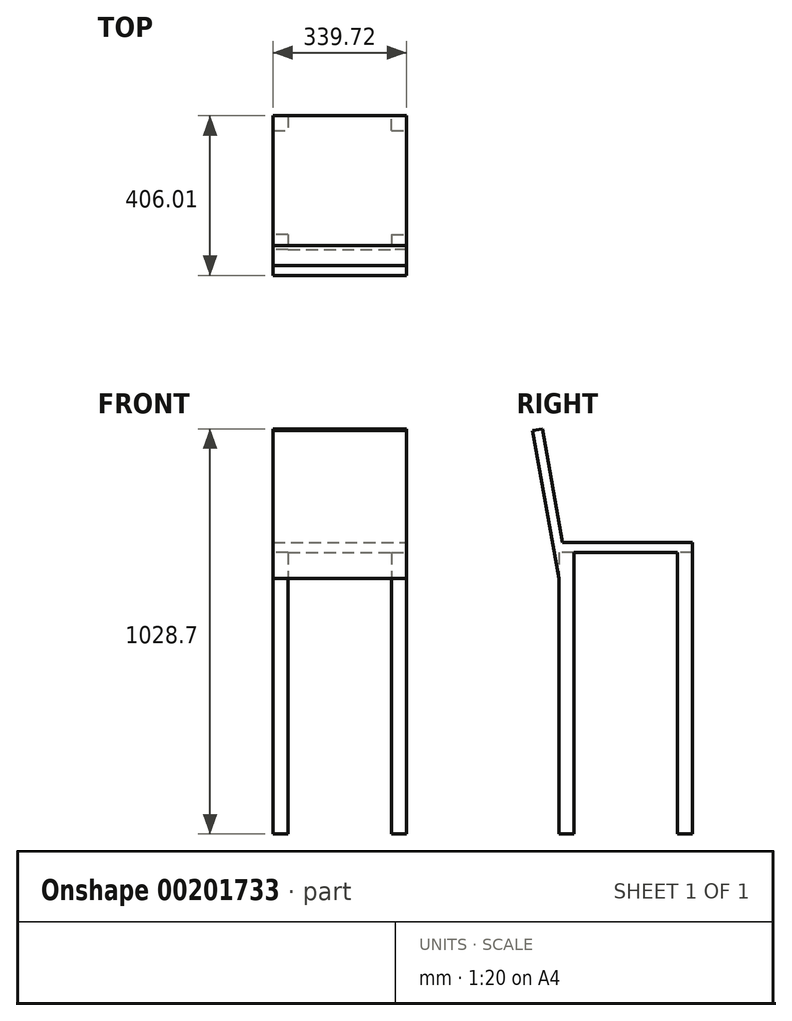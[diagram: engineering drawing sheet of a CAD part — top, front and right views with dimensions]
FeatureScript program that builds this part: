
annotation { "Feature Type Name" : "Feature", "Feature Type Description" : "" }
export const myFeature = defineFeature(function(context is Context, id is Id, definition is map)
    precondition{}
    {
        {
            var Q0;
            Q0=qCreatedBy(makeId("Top.planeOp"),FACE);
            var sketch = newSketch(context, id + "F0", { "sketchPlane" : qUnion([Q0])});
            skLineSegment(sketch, "E0.bottom", {"start": v(169.86, -169.86) * mm, "end": v(-169.86, -169.86) * mm, "construction": true});
            skLineSegment(sketch, "E0.top", {"start": v(169.86, 169.86) * mm, "end": v(-169.86, 169.86) * mm, "construction": true});
            skLineSegment(sketch, "E0.left", {"start": v(169.86, -169.86) * mm, "end": v(169.86, 169.86) * mm, "construction": true});
            skLineSegment(sketch, "E0.right", {"start": v(-169.86, -169.86) * mm, "end": v(-169.86, 169.86) * mm, "construction": true});
            skPoint(sketch, "E0.middle", {"position": v(0, 0) * mm});
            skLineSegment(sketch, "E1.bottom", {"start": v(-169.86, 169.86) * mm, "end": v(-131.76, 169.86) * mm});
            skLineSegment(sketch, "E1.top", {"start": v(-169.86, 131.76) * mm, "end": v(-131.76, 131.76) * mm});
            skLineSegment(sketch, "E1.left", {"start": v(-169.86, 169.86) * mm, "end": v(-169.86, 131.76) * mm});
            skLineSegment(sketch, "E1.right", {"start": v(-131.76, 169.86) * mm, "end": v(-131.76, 131.76) * mm});
            skLineSegment(sketch, "E2.bottom", {"start": v(-169.86, -169.86) * mm, "end": v(-131.76, -169.86) * mm});
            skLineSegment(sketch, "E2.top", {"start": v(-169.86, -131.76) * mm, "end": v(-131.76, -131.76) * mm});
            skLineSegment(sketch, "E2.left", {"start": v(-169.86, -169.86) * mm, "end": v(-169.86, -131.76) * mm});
            skLineSegment(sketch, "E2.right", {"start": v(-131.76, -169.86) * mm, "end": v(-131.76, -131.76) * mm});
            skLineSegment(sketch, "E3.bottom", {"start": v(169.86, -169.86) * mm, "end": v(131.76, -169.86) * mm});
            skLineSegment(sketch, "E3.top", {"start": v(169.86, -131.76) * mm, "end": v(131.76, -131.76) * mm});
            skLineSegment(sketch, "E3.left", {"start": v(169.86, -169.86) * mm, "end": v(169.86, -131.76) * mm});
            skLineSegment(sketch, "E3.right", {"start": v(131.76, -169.86) * mm, "end": v(131.76, -131.76) * mm});
            skLineSegment(sketch, "E4.bottom", {"start": v(169.86, 169.86) * mm, "end": v(131.76, 169.86) * mm});
            skLineSegment(sketch, "E4.top", {"start": v(169.86, 131.76) * mm, "end": v(131.76, 131.76) * mm});
            skLineSegment(sketch, "E4.left", {"start": v(169.86, 169.86) * mm, "end": v(169.86, 131.76) * mm});
            skLineSegment(sketch, "E4.right", {"start": v(131.76, 169.86) * mm, "end": v(131.76, 131.76) * mm});
            skSolve(sketch);
        }
        {
            var Q0;
            Q0=makeQuery(id+"F0.imprint","IMPRINT",FACE,{"disambiguationData":[TD([[makeQuery(id+"F0.imprint","IMPRINT",EDGE,{"derivedFrom":sQuery(id+"F0.wireOp",EDGE,"E1.bottom")}),-1.0]])]});
            var Q1;
            Q1=makeQuery(id+"F0.imprint","IMPRINT",FACE,{"disambiguationData":[TD([[makeQuery(id+"F0.imprint","IMPRINT",EDGE,{"derivedFrom":sQuery(id+"F0.wireOp",EDGE,"E2.bottom")}),1.0]])]});
            var Q2;
            Q2=makeQuery(id+"F0.imprint","IMPRINT",FACE,{"disambiguationData":[TD([[makeQuery(id+"F0.imprint","IMPRINT",EDGE,{"derivedFrom":sQuery(id+"F0.wireOp",EDGE,"E3.bottom")}),-1.0]])]});
            var Q3;
            Q3=makeQuery(id+"F0.imprint","IMPRINT",FACE,{"disambiguationData":[TD([[makeQuery(id+"F0.imprint","IMPRINT",EDGE,{"derivedFrom":sQuery(id+"F0.wireOp",EDGE,"E4.bottom")}),1.0]])]});
            extrude(context, id + "F1", {"entities" : qUnion([Q0, Q1, Q2, Q3]), "depth" : 739.77 * mm});
        }
        {
            var Q0;
            Q0=makeQuery(id+"F1.opExtrude","CAP_FACE",FACE,{"disambiguationData":[OSD([sQuery(id+"F0.wireOp",EDGE,"E1.bottom"),sQuery(id+"F0.wireOp",EDGE,"E1.top"),sQuery(id+"F0.wireOp",EDGE,"E1.left"),sQuery(id+"F0.wireOp",EDGE,"E1.right")])],"isStart":false});
            var sketch = newSketch(context, id + "F2", { "sketchPlane" : qUnion([Q0])});
            skPoint(sketch, "E5.0", {"position": v(-169.86, 150.81) * mm});
            skPoint(sketch, "E6.0", {"position": v(-169.86, 169.86) * mm});
            skPoint(sketch, "E7.0", {"position": v(-169.86, -169.86) * mm});
            skPoint(sketch, "E8.0", {"position": v(169.86, -169.86) * mm});
            skPoint(sketch, "E9.0", {"position": v(169.86, 169.86) * mm});
            skLineSegment(sketch, "E10.bottom", {"start": v(-169.86, 169.86) * mm, "end": v(169.86, 169.86) * mm});
            skLineSegment(sketch, "E10.top", {"start": v(-169.86, -169.86) * mm, "end": v(169.86, -169.86) * mm});
            skLineSegment(sketch, "E10.left", {"start": v(-169.86, 169.86) * mm, "end": v(-169.86, -169.86) * mm});
            skLineSegment(sketch, "E10.right", {"start": v(169.86, 169.86) * mm, "end": v(169.86, -169.86) * mm});
            skSolve(sketch);
        }
        {
            var Q0;
            {var subQ2=sQuery(id+"F2.wireOp",EDGE,"E10.top");Q0=makeQuery(id+"F2.imprint","IMPRINT",FACE,{"disambiguationData":[TD([[makeQuery(id+"F2.imprint","IMPRINT",EDGE,{"derivedFrom":subQ2}),1.0]])]});}
            extrude(context, id + "F3", {"entities" : qUnion([Q0]), "oppositeDirection" : true, "depth" : 25.4 * mm});
        }
        {
            var Q0;
            Q0=makeQuery(id+"F3.opExtrude","SWEPT_BODY",BODY,{"disambiguationData":[OSD([sQuery(id+"F0.wireOp",EDGE,"E1.top"),sQuery(id+"F0.wireOp",EDGE,"E1.right"),sQuery(id+"F2.wireOp",EDGE,"E10.bottom"),sQuery(id+"F2.wireOp",EDGE,"E10.top"),sQuery(id+"F2.wireOp",EDGE,"E10.left"),sQuery(id+"F2.wireOp",EDGE,"E10.right")])]});
            var Q1;
            Q1=makeQuery(id+"F1.opExtrude","SWEPT_BODY",BODY,{"disambiguationData":[OSD([sQuery(id+"F0.wireOp",EDGE,"E1.bottom"),sQuery(id+"F0.wireOp",EDGE,"E1.top"),sQuery(id+"F0.wireOp",EDGE,"E1.left"),sQuery(id+"F0.wireOp",EDGE,"E1.right")])]});
            var Q2;
            Q2=makeQuery(id+"F1.opExtrude","SWEPT_BODY",BODY,{"disambiguationData":[OSD([sQuery(id+"F0.wireOp",EDGE,"E4.bottom"),sQuery(id+"F0.wireOp",EDGE,"E4.top"),sQuery(id+"F0.wireOp",EDGE,"E4.left"),sQuery(id+"F0.wireOp",EDGE,"E4.right")])]});
            var Q3;
            Q3=makeQuery(id+"F1.opExtrude","SWEPT_BODY",BODY,{"disambiguationData":[OSD([sQuery(id+"F0.wireOp",EDGE,"E3.bottom"),sQuery(id+"F0.wireOp",EDGE,"E3.top"),sQuery(id+"F0.wireOp",EDGE,"E3.left"),sQuery(id+"F0.wireOp",EDGE,"E3.right")])]});
            var Q4;
            Q4=makeQuery(id+"F1.opExtrude","SWEPT_BODY",BODY,{"disambiguationData":[OSD([sQuery(id+"F0.wireOp",EDGE,"E2.bottom"),sQuery(id+"F0.wireOp",EDGE,"E2.top"),sQuery(id+"F0.wireOp",EDGE,"E2.left"),sQuery(id+"F0.wireOp",EDGE,"E2.right")])]});
            booleanBodies(context, id + "F4", {"operationType" : BooleanOperationType.UNION, "tools" : qUnion([Q0, Q1, Q2, Q3, Q4])});
        }
        {
            var Q0;
            Q0=qCreatedBy(makeId("Right.planeOp"),FACE);
            var sketch = newSketch(context, id + "F5", { "sketchPlane" : qUnion([Q0])});
            skPoint(sketch, "E11.0", {"position": v(-169.86, 739.78) * mm});
            skLineSegment(sketch, "E12.0", {"start": v(169.86, 739.78) * mm, "end": v(-169.86, 739.78) * mm, "construction": true});
            skLineSegment(sketch, "E13.0", {"start": v(-169.86, 0) * mm, "end": v(-169.86, 739.78) * mm, "construction": true});
            skLineSegment(sketch, "E14", {"start": v(-160.2, 739.78) * mm, "end": v(-211.14, 1028.7) * mm});
            skLineSegment(sketch, "E15", {"start": v(-211.14, 1028.7) * mm, "end": v(-236.15, 1024.29) * mm});
            skLineSegment(sketch, "E16", {"start": v(-236.15, 1024.29) * mm, "end": v(-169.86, 648.35) * mm});
            skLineSegment(sketch, "E17", {"start": v(-169.86, 648.35) * mm, "end": v(-169.86, 739.78) * mm});
            skLineSegment(sketch, "E18", {"start": v(-169.86, 739.78) * mm, "end": v(-160.2, 739.78) * mm});
            skSolve(sketch);
        }
        {
            var Q0;
            Q0=makeQuery(id+"F5.imprint","IMPRINT",FACE,{"disambiguationData":[TD([[makeQuery(id+"F5.imprint","IMPRINT",EDGE,{"derivedFrom":sQuery(id+"F5.wireOp",EDGE,"E14")}),1.0]])]});
            var Q1;
            Q1=makeQuery(id+"F4.opBoolean","MERGE",FACE,{"derivedFrom":[makeQuery(id+"F1.opExtrude","SWEPT_FACE",FACE,{"disambiguationData":[OSD([sQuery(id+"F0.wireOp",EDGE,"E3.left")])]}),makeQuery(id+"F1.opExtrude","SWEPT_FACE",FACE,{"disambiguationData":[OSD([sQuery(id+"F0.wireOp",EDGE,"E4.left")])]}),makeQuery(id+"F3.opExtrude","SWEPT_FACE",FACE,{"disambiguationData":[OSD([sQuery(id+"F2.wireOp",EDGE,"E10.right")])]})]});
            var Q2;
            Q2=makeQuery(id+"F4.opBoolean","MERGE",FACE,{"derivedFrom":[makeQuery(id+"F1.opExtrude","SWEPT_FACE",FACE,{"disambiguationData":[OSD([sQuery(id+"F0.wireOp",EDGE,"E1.left")])]}),makeQuery(id+"F1.opExtrude","SWEPT_FACE",FACE,{"disambiguationData":[OSD([sQuery(id+"F0.wireOp",EDGE,"E2.left")])]}),makeQuery(id+"F3.opExtrude","SWEPT_FACE",FACE,{"disambiguationData":[OSD([sQuery(id+"F2.wireOp",EDGE,"E10.left")])]})]});
            extrude(context, id + "F6", {"entities" : qUnion([Q0]), "operationType" : NewBodyOperationType.ADD, "endBound" : BoundingType.UP_TO_SURFACE, "endBoundEntityFace" : qUnion([Q1]), "depth" : 25.4 * mm, "hasSecondDirection" : true, "secondDirectionBound" : SecondDirectionBoundingType.UP_TO_SURFACE, "secondDirectionOppositeDirection" : true, "secondDirectionBoundEntityFace" : qUnion([Q2]), "secondDirectionDepth" : 25.4 * mm});
        }
    });
